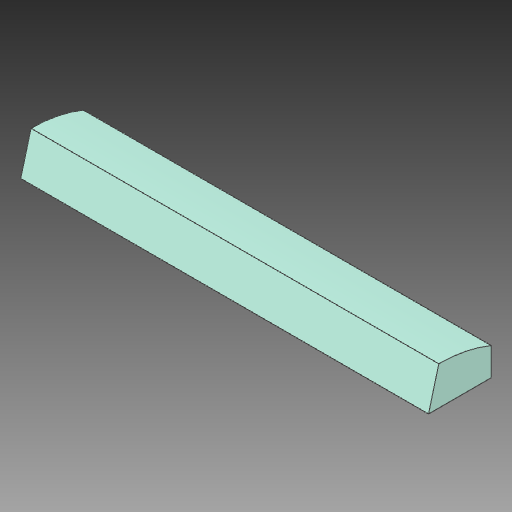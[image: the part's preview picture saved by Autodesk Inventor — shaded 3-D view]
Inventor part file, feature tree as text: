
AUTODESK INVENTOR PART (.ipt)
format: ipt  version: 2018 (Build 220112000, 112)  size: 145,920 bytes
history: native  units: mm
features: extrude x4, other x4, shell x1, sketch x1
ambient origin geometry x8: Origin, YZ Plane, XZ Plane, XY Plane, X Axis, Y Axis, Z Axis, Center Point
bodies: Solid1 (feature_tree)
feature tree (10):
  extrude  "Spacebar Bulk"  Depth=5.0mm
  extrude  "Curve Cutaway"  Depth=5.0mm TaperAngle=0.0deg
  shell  "Inner Shell"  Thickness=15.0deg
  other  "PoleBase Plane"
  extrude  "Pole Extrusion"  Depth=5.0mm TaperAngle=0.0deg
  extrude  "Extrusion4"  Depth=5.0mm
  other  "Spacebar base"
  other  "Curve Profile"
  other  "Center Circle"
  sketch  "Sketch4"  dims[d0=117.0mm d1=18.0mm d2=11.0mm d3=0.0mm d4=15.0deg d7=11.0mm d8=0.0mm d9=8.0mm d10=1.5mm d11=5.3mm d12=11.0mm d13=0.0mm d14=4.15mm d15=1.1mm d16=1.1mm d17=4.15mm d18=5.0mm d19=0.0mm]
